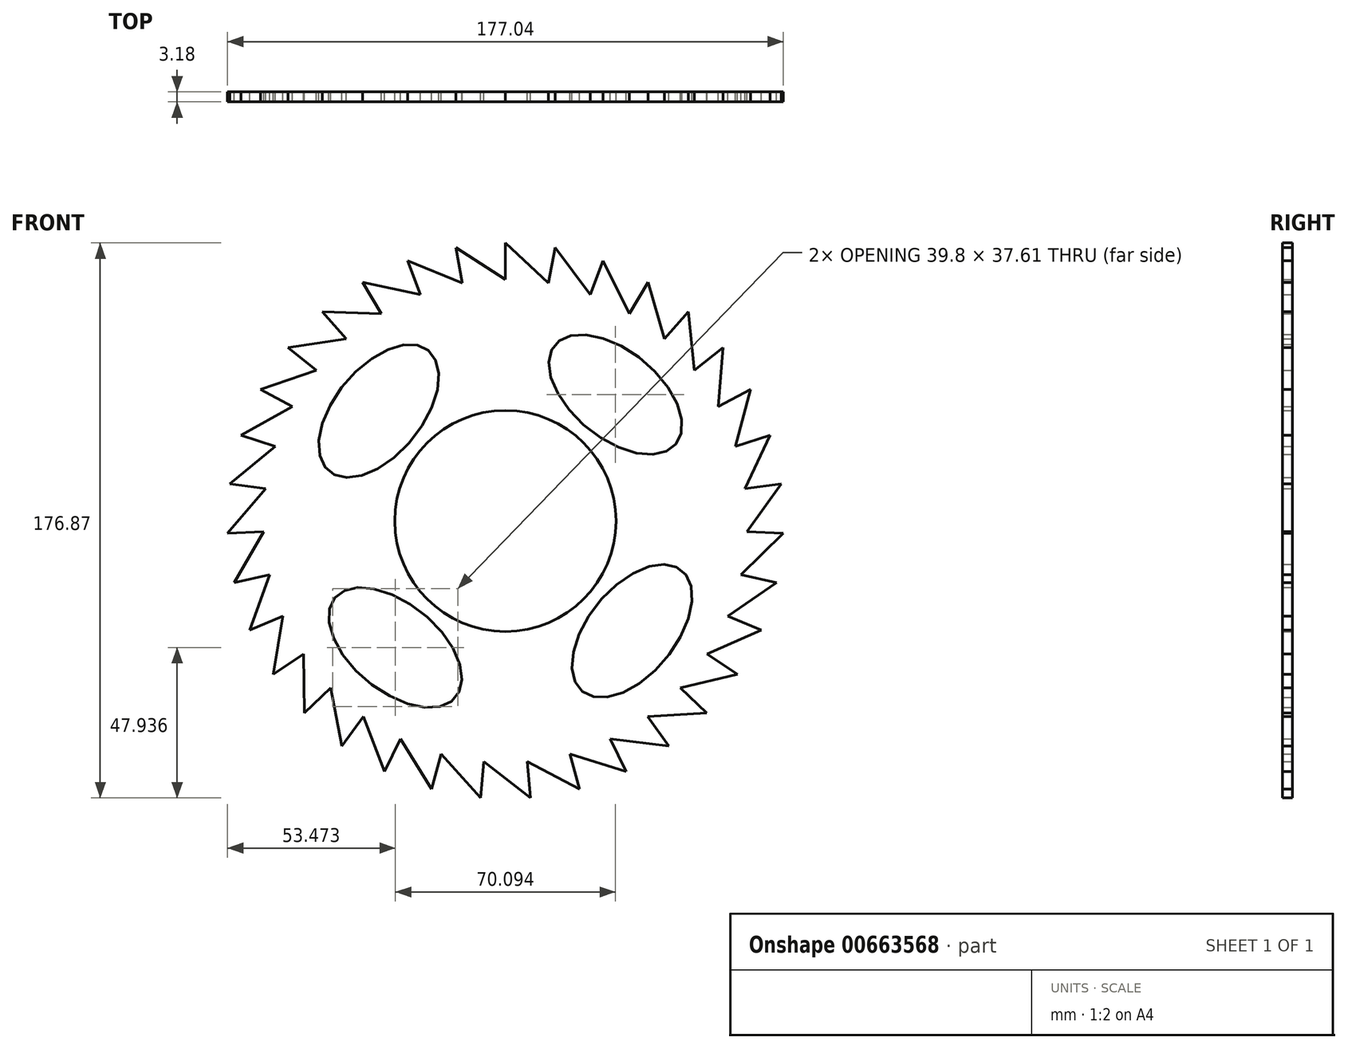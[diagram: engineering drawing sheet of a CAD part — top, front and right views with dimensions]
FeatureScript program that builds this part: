
annotation { "Feature Type Name" : "Feature", "Feature Type Description" : "" }
export const myFeature = defineFeature(function(context is Context, id is Id, definition is map)
    precondition{}
    {
        {
            var Q0;
            Q0=qCreatedBy(makeId("Front.planeOp"),FACE);
            var sketch = newSketch(context, id + "F0", { "sketchPlane" : qUnion([Q0])});
            skCircle(sketch, "E0", {"center": v(0, 0) * mm, "radius": 76.2 * mm, "construction": true});
            skCircle(sketch, "E1", {"center": v(0, 0) * mm, "radius": 35.22 * mm});
            skEllipse(sketch, "E2", {"center": v(-40.32, 35.05) * mm, "majorRadius": 24.96 * mm, "minorRadius": 13.94 * mm, "majorAxis": v(0.63, 0.77)});
            skEllipse(sketch, "E3.1.0", {"center": v(-35.05, -40.32) * mm, "majorRadius": 24.96 * mm, "minorRadius": 13.94 * mm, "majorAxis": v(-0.77, 0.63)});
            skEllipse(sketch, "E3.2.0", {"center": v(40.32, -35.05) * mm, "majorRadius": 24.96 * mm, "minorRadius": 13.94 * mm, "majorAxis": v(-0.63, -0.77)});
            skEllipse(sketch, "E3.3.0", {"center": v(35.05, 40.32) * mm, "majorRadius": 24.96 * mm, "minorRadius": 13.94 * mm, "majorAxis": v(0.77, -0.63)});
            skLineSegment(sketch, "E4", {"start": v(0, 76.2) * mm, "end": v(0, 88.61) * mm});
            skLineSegment(sketch, "E5", {"start": v(0, 88.61) * mm, "end": v(14.89, 74.73) * mm});
            skLineSegment(sketch, "E6.1.0", {"start": v(-13.6, 74.98) * mm, "end": v(-15.82, 87.19) * mm});
            skLineSegment(sketch, "E6.1.1", {"start": v(-15.82, 87.19) * mm, "end": v(1.3, 76.19) * mm});
            skLineSegment(sketch, "E6.2.0", {"start": v(-26.77, 71.34) * mm, "end": v(-31.14, 82.96) * mm});
            skLineSegment(sketch, "E6.2.1", {"start": v(-31.14, 82.96) * mm, "end": v(-12.32, 75.2) * mm});
            skLineSegment(sketch, "E6.3.0", {"start": v(-39.08, 65.41) * mm, "end": v(-45.45, 76.07) * mm});
            skLineSegment(sketch, "E6.3.1", {"start": v(-45.45, 76.07) * mm, "end": v(-25.55, 71.79) * mm});
            skLineSegment(sketch, "E6.4.0", {"start": v(-50.13, 57.38) * mm, "end": v(-58.3, 66.73) * mm});
            skLineSegment(sketch, "E6.4.1", {"start": v(-58.3, 66.73) * mm, "end": v(-37.96, 66.07) * mm});
            skLineSegment(sketch, "E6.5.0", {"start": v(-59.58, 47.5) * mm, "end": v(-69.28, 55.25) * mm});
            skLineSegment(sketch, "E6.5.1", {"start": v(-69.28, 55.25) * mm, "end": v(-49.15, 58.23) * mm});
            skLineSegment(sketch, "E6.6.0", {"start": v(-67.1, 36.1) * mm, "end": v(-78.03, 42) * mm});
            skLineSegment(sketch, "E6.6.1", {"start": v(-78.03, 42) * mm, "end": v(-58.75, 48.52) * mm});
            skLineSegment(sketch, "E6.7.0", {"start": v(-72.47, 23.55) * mm, "end": v(-84.28, 27.38) * mm});
            skLineSegment(sketch, "E6.7.1", {"start": v(-84.28, 27.38) * mm, "end": v(-66.47, 37.25) * mm});
            skLineSegment(sketch, "E6.8.0", {"start": v(-75.51, 10.23) * mm, "end": v(-87.81, 11.9) * mm});
            skLineSegment(sketch, "E6.8.1", {"start": v(-87.81, 11.9) * mm, "end": v(-72.06, 24.78) * mm});
            skLineSegment(sketch, "E6.9.0", {"start": v(-76.12, -3.42) * mm, "end": v(-88.52, -3.98) * mm});
            skLineSegment(sketch, "E6.9.1", {"start": v(-88.52, -3.98) * mm, "end": v(-75.32, 11.52) * mm});
            skLineSegment(sketch, "E6.10.0", {"start": v(-74.29, -16.96) * mm, "end": v(-86.4, -19.72) * mm});
            skLineSegment(sketch, "E6.10.1", {"start": v(-86.4, -19.72) * mm, "end": v(-76.17, -2.12) * mm});
            skLineSegment(sketch, "E6.11.0", {"start": v(-70.07, -29.95) * mm, "end": v(-81.48, -34.83) * mm});
            skLineSegment(sketch, "E6.11.1", {"start": v(-81.48, -34.83) * mm, "end": v(-74.57, -15.68) * mm});
            skLineSegment(sketch, "E6.12.0", {"start": v(-63.6, -41.98) * mm, "end": v(-73.95, -48.82) * mm});
            skLineSegment(sketch, "E6.12.1", {"start": v(-73.95, -48.82) * mm, "end": v(-70.57, -28.74) * mm});
            skLineSegment(sketch, "E6.13.0", {"start": v(-55.08, -52.66) * mm, "end": v(-64.05, -61.24) * mm});
            skLineSegment(sketch, "E6.13.1", {"start": v(-64.05, -61.24) * mm, "end": v(-64.3, -40.88) * mm});
            skLineSegment(sketch, "E6.14.0", {"start": v(-44.79, -61.65) * mm, "end": v(-52.09, -71.69) * mm});
            skLineSegment(sketch, "E6.14.1", {"start": v(-52.09, -71.69) * mm, "end": v(-55.97, -51.7) * mm});
            skLineSegment(sketch, "E6.15.0", {"start": v(-33.06, -68.65) * mm, "end": v(-38.45, -79.84) * mm});
            skLineSegment(sketch, "E6.15.1", {"start": v(-38.45, -79.84) * mm, "end": v(-45.84, -60.87) * mm});
            skLineSegment(sketch, "E6.16.0", {"start": v(-20.27, -73.45) * mm, "end": v(-23.57, -85.42) * mm});
            skLineSegment(sketch, "E6.16.1", {"start": v(-23.57, -85.42) * mm, "end": v(-34.23, -68.08) * mm});
            skLineSegment(sketch, "E6.17.0", {"start": v(-6.83, -75.9) * mm, "end": v(-7.94, -88.26) * mm});
            skLineSegment(sketch, "E6.17.1", {"start": v(-7.94, -88.26) * mm, "end": v(-21.53, -73.1) * mm});
            skLineSegment(sketch, "E6.18.0", {"start": v(6.83, -75.9) * mm, "end": v(7.94, -88.26) * mm});
            skLineSegment(sketch, "E6.18.1", {"start": v(7.94, -88.26) * mm, "end": v(-8.13, -75.77) * mm});
            skLineSegment(sketch, "E6.19.0", {"start": v(20.27, -73.45) * mm, "end": v(23.57, -85.42) * mm});
            skLineSegment(sketch, "E6.19.1", {"start": v(23.57, -85.42) * mm, "end": v(5.53, -76) * mm});
            skLineSegment(sketch, "E6.20.0", {"start": v(33.06, -68.65) * mm, "end": v(38.45, -79.84) * mm});
            skLineSegment(sketch, "E6.20.1", {"start": v(38.45, -79.84) * mm, "end": v(19.01, -73.8) * mm});
            skLineSegment(sketch, "E6.21.0", {"start": v(44.79, -61.65) * mm, "end": v(52.09, -71.69) * mm});
            skLineSegment(sketch, "E6.21.1", {"start": v(52.09, -71.69) * mm, "end": v(31.88, -69.2) * mm});
            skLineSegment(sketch, "E6.22.0", {"start": v(55.08, -52.66) * mm, "end": v(64.05, -61.24) * mm});
            skLineSegment(sketch, "E6.22.1", {"start": v(64.05, -61.24) * mm, "end": v(43.73, -62.4) * mm});
            skLineSegment(sketch, "E6.23.0", {"start": v(63.6, -41.98) * mm, "end": v(73.95, -48.82) * mm});
            skLineSegment(sketch, "E6.23.1", {"start": v(73.95, -48.82) * mm, "end": v(54.17, -53.6) * mm});
            skLineSegment(sketch, "E6.24.0", {"start": v(70.07, -29.95) * mm, "end": v(81.48, -34.83) * mm});
            skLineSegment(sketch, "E6.24.1", {"start": v(81.48, -34.83) * mm, "end": v(62.87, -43.06) * mm});
            skLineSegment(sketch, "E6.25.0", {"start": v(74.29, -16.96) * mm, "end": v(86.4, -19.72) * mm});
            skLineSegment(sketch, "E6.25.1", {"start": v(86.4, -19.72) * mm, "end": v(69.55, -31.14) * mm});
            skLineSegment(sketch, "E6.26.0", {"start": v(76.12, -3.42) * mm, "end": v(88.52, -3.98) * mm});
            skLineSegment(sketch, "E6.26.1", {"start": v(88.52, -3.98) * mm, "end": v(73.99, -18.23) * mm});
            skLineSegment(sketch, "E6.27.0", {"start": v(75.51, 10.23) * mm, "end": v(87.81, 11.9) * mm});
            skLineSegment(sketch, "E6.27.1", {"start": v(87.81, 11.9) * mm, "end": v(76.05, -4.72) * mm});
            skLineSegment(sketch, "E6.28.0", {"start": v(72.47, 23.55) * mm, "end": v(84.28, 27.38) * mm});
            skLineSegment(sketch, "E6.28.1", {"start": v(84.28, 27.38) * mm, "end": v(75.67, 8.93) * mm});
            skLineSegment(sketch, "E6.29.0", {"start": v(67.1, 36.1) * mm, "end": v(78.03, 42) * mm});
            skLineSegment(sketch, "E6.29.1", {"start": v(78.03, 42) * mm, "end": v(72.86, 22.3) * mm});
            skLineSegment(sketch, "E6.30.0", {"start": v(59.58, 47.5) * mm, "end": v(69.28, 55.25) * mm});
            skLineSegment(sketch, "E6.30.1", {"start": v(69.28, 55.25) * mm, "end": v(67.7, 34.95) * mm});
            skLineSegment(sketch, "E6.31.0", {"start": v(50.13, 57.38) * mm, "end": v(58.3, 66.73) * mm});
            skLineSegment(sketch, "E6.31.1", {"start": v(58.3, 66.73) * mm, "end": v(60.38, 46.48) * mm});
            skLineSegment(sketch, "E6.32.0", {"start": v(39.08, 65.41) * mm, "end": v(45.45, 76.07) * mm});
            skLineSegment(sketch, "E6.32.1", {"start": v(45.45, 76.07) * mm, "end": v(51.1, 56.52) * mm});
            skLineSegment(sketch, "E6.33.0", {"start": v(26.77, 71.34) * mm, "end": v(31.14, 82.96) * mm});
            skLineSegment(sketch, "E6.33.1", {"start": v(31.14, 82.96) * mm, "end": v(40.2, 64.74) * mm});
            skLineSegment(sketch, "E6.34.0", {"start": v(13.6, 74.98) * mm, "end": v(15.82, 87.19) * mm});
            skLineSegment(sketch, "E6.34.1", {"start": v(15.82, 87.19) * mm, "end": v(28, 70.87) * mm});
            skSolve(sketch);
        }
        {
            var Q0;
            Q0 = qSketchRegion(id + "F0", true);
            extrude(context, id + "F1", {"entities" : qUnion([Q0]), "depth" : 3.17 * mm, "offsetDistance" : 25.4 * mm});
        }
    });
